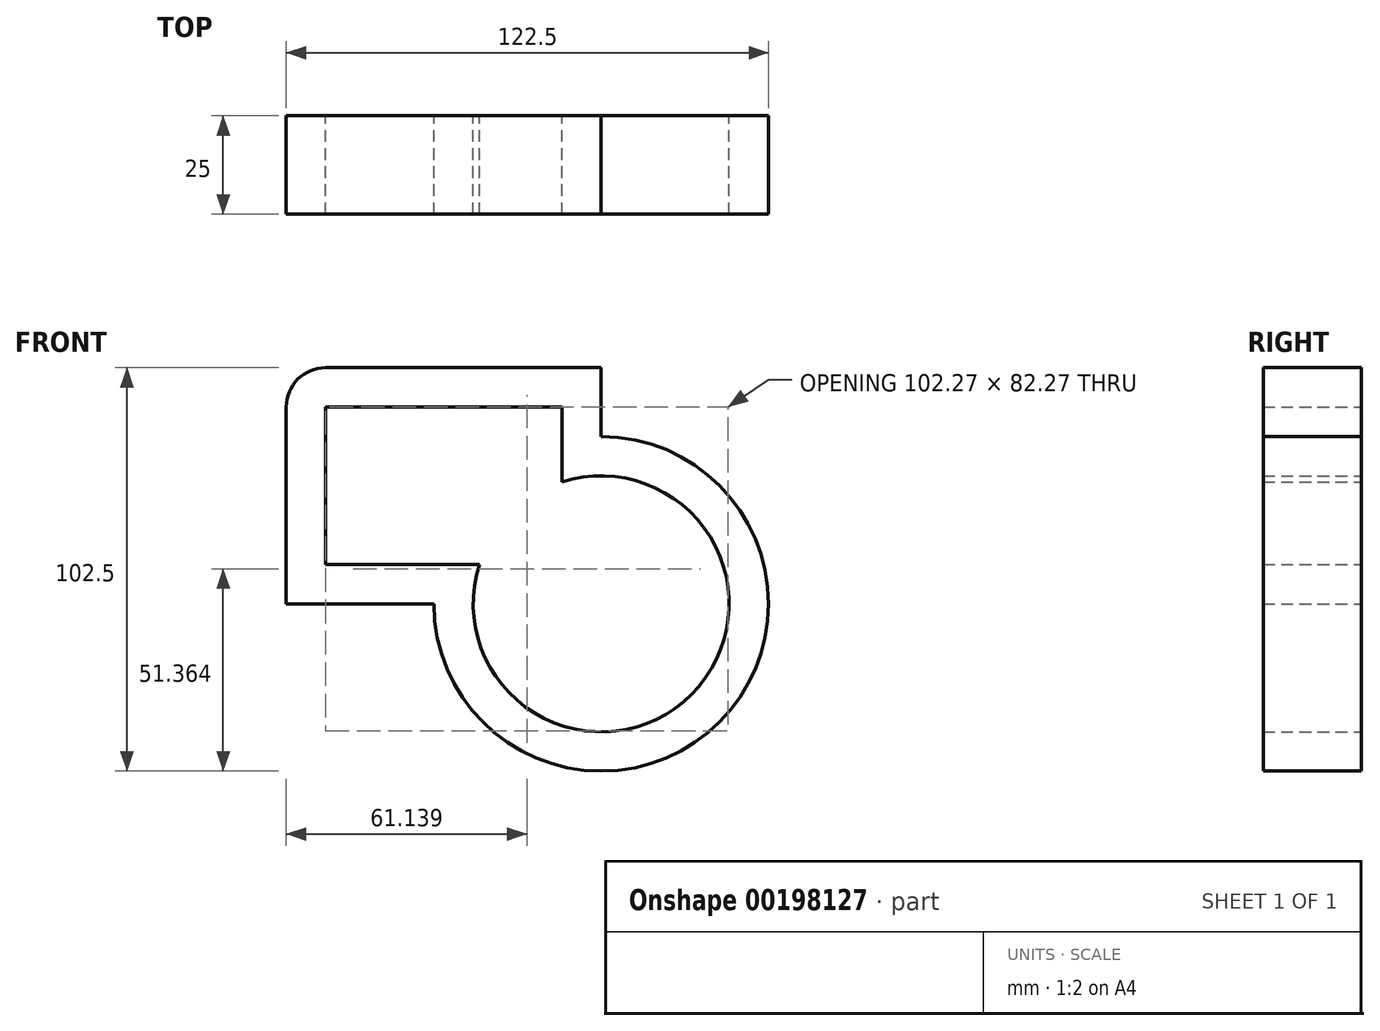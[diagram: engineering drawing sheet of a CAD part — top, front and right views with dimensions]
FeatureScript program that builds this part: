
annotation { "Feature Type Name" : "Feature", "Feature Type Description" : "" }
export const myFeature = defineFeature(function(context is Context, id is Id, definition is map)
    precondition{}
    {
        {
            var Q0;
            Q0=qCreatedBy(makeId("Front.planeOp"),FACE);
            var sketch = newSketch(context, id + "F0", { "sketchPlane" : qUnion([Q0])});
            skLineSegment(sketch, "E0.bottom", {"start": v(-50.92, 36.8) * mm, "end": v(19.08, 36.8) * mm});
            skLineSegment(sketch, "E0.top", {"start": v(-60.92, -23.2) * mm, "end": v(-23.42, -23.2) * mm});
            skLineSegment(sketch, "E0.left", {"start": v(-60.92, 26.8) * mm, "end": v(-60.92, -23.2) * mm});
            skLineSegment(sketch, "E0.right", {"start": v(19.08, 36.8) * mm, "end": v(19.08, 19.3) * mm});
            skArc(sketch, "E1", {"start": v(-23.42, -23.2) * mm, "mid": v(49.13, -53.25) * mm, "end": v(19.08, 19.3) * mm});
            skPoint(sketch, "E2.visualSharp", {"position": v(-60.92, 36.8) * mm});
            skArc(sketch, "E2.filletArc", {"start": v(-50.92, 36.8) * mm, "mid": v(-57.99, 33.87) * mm, "end": v(-60.92, 26.8) * mm});
            skLineSegment(sketch, "E3.0", {"start": v(-50.92, 26.8) * mm, "end": v(-50.92, -13.2) * mm});
            skArc(sketch, "E3.1", {"start": v(-11.84, -13.2) * mm, "mid": v(42.06, -46.18) * mm, "end": v(9.08, 7.72) * mm});
            skLineSegment(sketch, "E3.2", {"start": v(9.08, 26.8) * mm, "end": v(9.08, 7.72) * mm});
            skLineSegment(sketch, "E3.3", {"start": v(-50.92, -13.2) * mm, "end": v(-11.84, -13.2) * mm});
            skLineSegment(sketch, "E3.4", {"start": v(-50.92, 26.8) * mm, "end": v(9.08, 26.8) * mm});
            skLineSegment(sketch, "E3.5", {"start": v(-50.92, 26.8) * mm, "end": v(-50.92, 26.8) * mm});
            skSolve(sketch);
        }
        {
            var Q0;
            Q0=makeQuery(id+"F0.imprint","IMPRINT",FACE,{"disambiguationData":[TD([[makeQuery(id+"F0.imprint","IMPRINT",EDGE,{"derivedFrom":sQuery(id+"F0.wireOp",EDGE,"E0.bottom")}),-1.0]])]});
            extrude(context, id + "F1", {"entities" : qUnion([Q0]), "depth" : 25 * mm});
        }
    });
